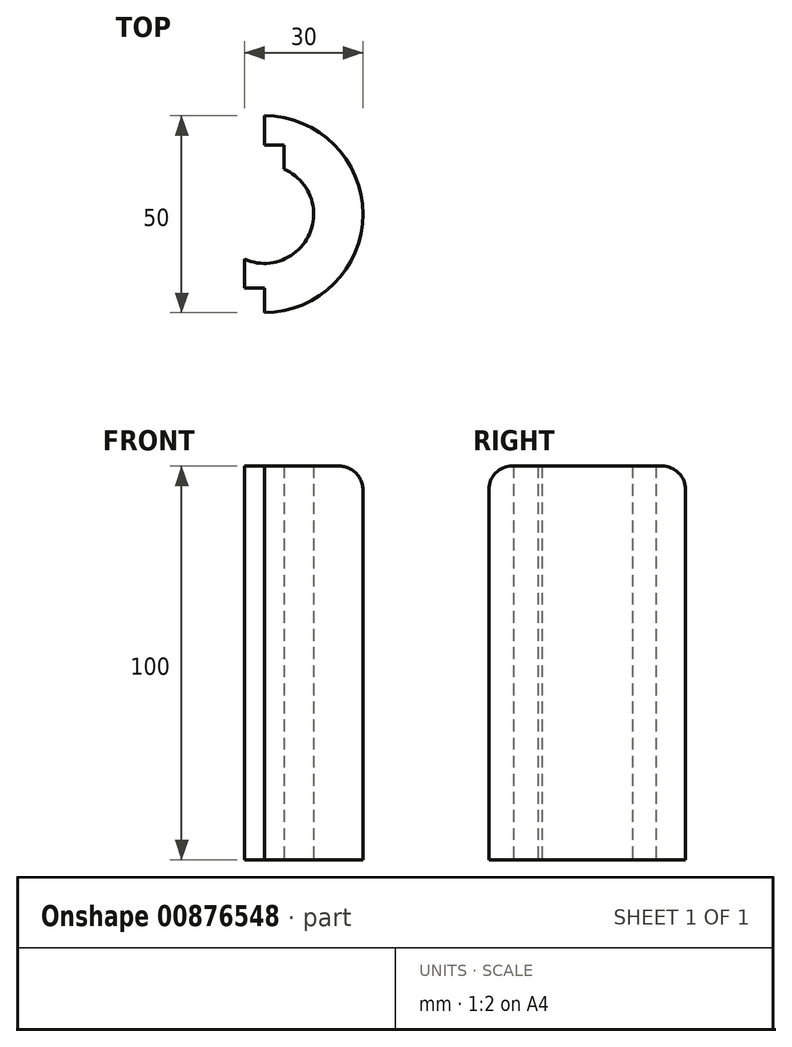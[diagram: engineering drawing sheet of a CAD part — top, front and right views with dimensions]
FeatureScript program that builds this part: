
annotation { "Feature Type Name" : "Feature", "Feature Type Description" : "" }
export const myFeature = defineFeature(function(context is Context, id is Id, definition is map)
    precondition{}
    {
        {
            var Q0;
            Q0=qCreatedBy(makeId("Top.planeOp"),FACE);
            var sketch = newSketch(context, id + "F0", { "sketchPlane" : qUnion([Q0])});
            skArc(sketch, "E0", {"start": v(0, -12.5) * mm, "mid": v(12.24, -2.55) * mm, "end": v(5, 11.46) * mm});
            skArc(sketch, "E1", {"start": v(5, -24.5) * mm, "mid": v(24.87, 2.51) * mm, "end": v(0, 25) * mm});
            skLineSegment(sketch, "E2", {"start": v(0, 17.5) * mm, "end": v(0, 25) * mm});
            skLineSegment(sketch, "E3", {"start": v(0, 17.5) * mm, "end": v(5, 17.5) * mm});
            skLineSegment(sketch, "E4", {"start": v(5, 17.5) * mm, "end": v(5, 11.46) * mm});
            skArc(sketch, "E5", {"start": v(-5, -11.46) * mm, "mid": v(11.46, -5) * mm, "end": v(5, 11.46) * mm});
            skArc(sketch, "E6", {"start": v(0, -25) * mm, "mid": v(25, 0) * mm, "end": v(0, 25) * mm});
            skLineSegment(sketch, "E7", {"start": v(0, -18.75) * mm, "end": v(0, -25) * mm});
            skLineSegment(sketch, "E8", {"start": v(0, -18.75) * mm, "end": v(-5, -18.75) * mm});
            skLineSegment(sketch, "E9", {"start": v(-5, -18.75) * mm, "end": v(-5, -11.46) * mm});
            skSolve(sketch);
        }
        {
            var Q0;
            Q0 = qSketchRegion(id + "F0", true);
            extrude(context, id + "F1", {"entities" : qUnion([Q0]), "depth" : 100 * mm, "offsetDistance" : 25 * mm});
        }
        {
            var Q0;
            Q0=makeQuery(id+"F1.opExtrude","CAP_EDGE",EDGE,{"disambiguationData":[OSD([sQuery(id+"F0.wireOp",EDGE,"E6")])],"isStart":false});
            fillet(context, id + "F2", {"entities" : qUnion([Q0]), "radius" : 6 * mm, "tangentPropagation" : true, "allowEdgeOverflow" : false});
        }
    });
